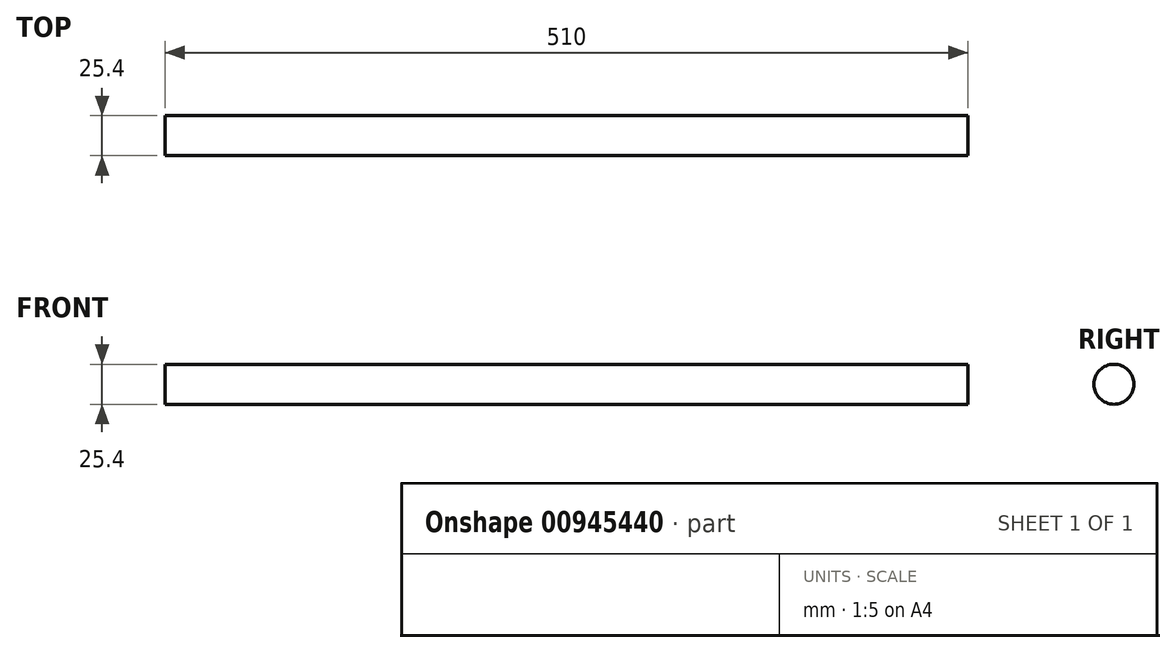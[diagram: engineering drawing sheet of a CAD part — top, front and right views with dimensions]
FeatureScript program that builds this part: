
annotation { "Feature Type Name" : "Feature", "Feature Type Description" : "" }
export const myFeature = defineFeature(function(context is Context, id is Id, definition is map)
    precondition{}
    {
        {
            var Q0;
            Q0=qCreatedBy(makeId("Right.planeOp"),FACE);
            var sketch = newSketch(context, id + "F0", { "sketchPlane" : qUnion([Q0])});
            skCircle(sketch, "E0", {"center": v(0, 0) * mm, "radius": 12.7 * mm});
            skSolve(sketch);
        }
        {
            var Q0;
            Q0=sQuery(id+"F0.wireOp",EDGE,"E0");
            extrude(context, id + "F1", {"bodyType" : ToolBodyType.SURFACE, "surfaceEntities" : qUnion([Q0]), "depth" : 510 * mm, "offsetDistance" : 25.4 * mm});
        }
    });
